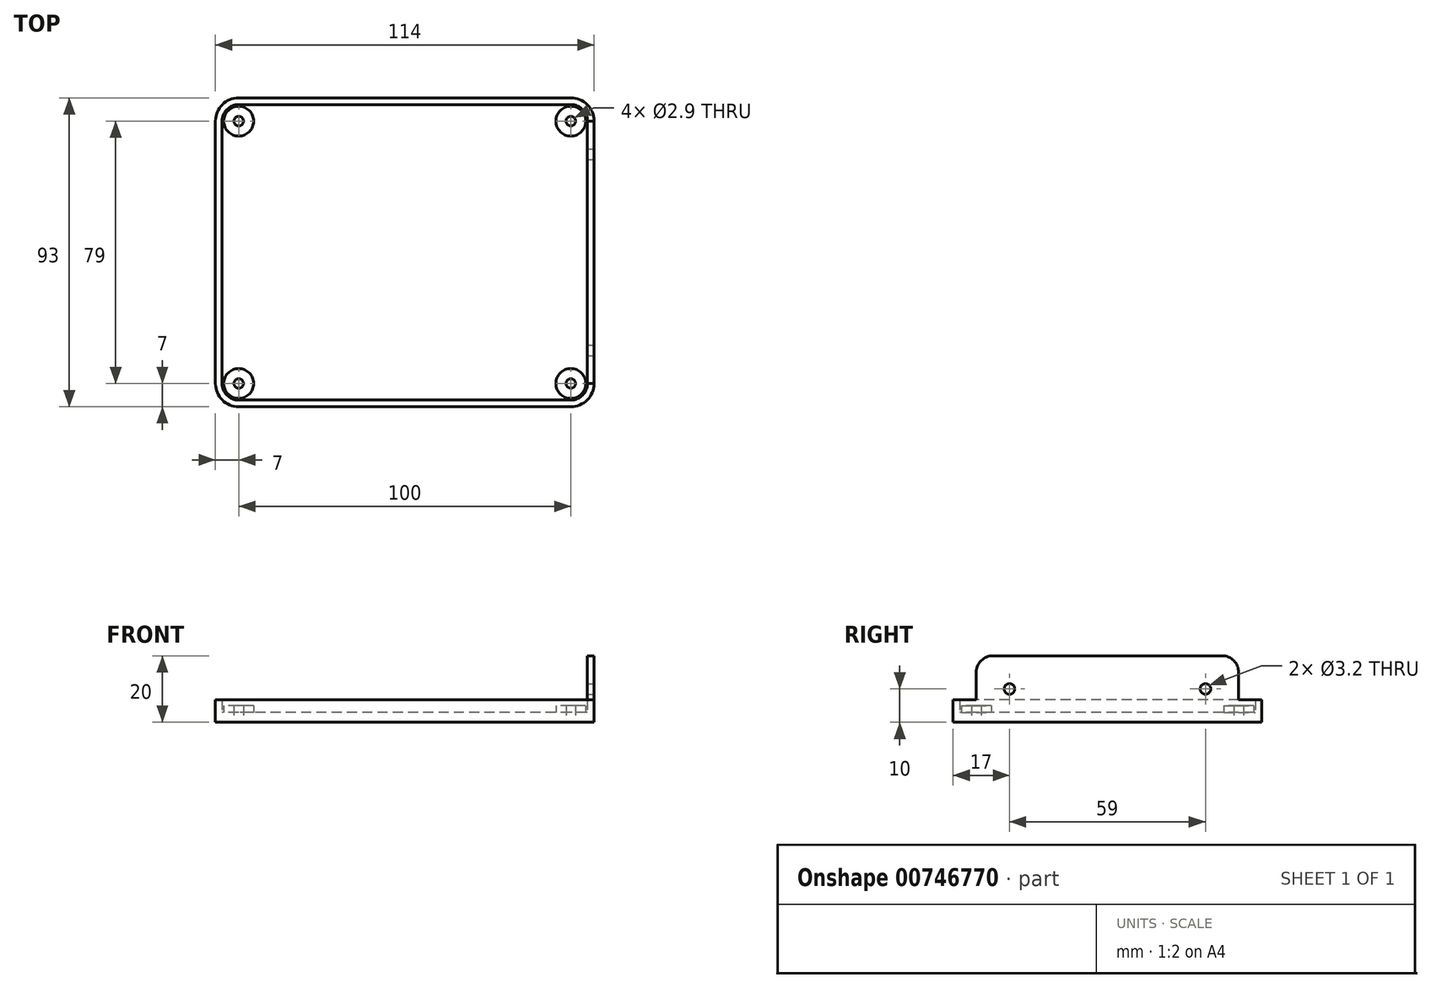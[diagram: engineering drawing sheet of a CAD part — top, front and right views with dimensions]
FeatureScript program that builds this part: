
annotation { "Feature Type Name" : "Feature", "Feature Type Description" : "" }
export const myFeature = defineFeature(function(context is Context, id is Id, definition is map)
    precondition{}
    {
        {
            var Q0;
            Q0=qCreatedBy(makeId("Top.planeOp"),FACE);
            var sketch = newSketch(context, id + "F0", { "sketchPlane" : qUnion([Q0])});
            skLineSegment(sketch, "E0.bottom", {"start": v(50, 44.5) * mm, "end": v(-50, 44.5) * mm});
            skLineSegment(sketch, "E0.top", {"start": v(50, -44.5) * mm, "end": v(-50, -44.5) * mm});
            skLineSegment(sketch, "E0.left", {"start": v(55, 39.5) * mm, "end": v(55, -39.5) * mm});
            skLineSegment(sketch, "E0.right", {"start": v(-55, 39.5) * mm, "end": v(-55, -39.5) * mm});
            skPoint(sketch, "E0.middle", {"position": v(0, 0) * mm});
            skCircle(sketch, "E1", {"center": v(-50, 39.5) * mm, "radius": 1.45 * mm});
            skCircle(sketch, "E2", {"center": v(-50, 39.5) * mm, "radius": 4.5 * mm});
            skCircle(sketch, "E3.0.1.0", {"center": v(-50, -39.5) * mm, "radius": 1.45 * mm});
            skCircle(sketch, "E3.0.1.1", {"center": v(-50, -39.5) * mm, "radius": 4.5 * mm});
            skCircle(sketch, "E3.1.0.0", {"center": v(50, 39.5) * mm, "radius": 1.45 * mm});
            skCircle(sketch, "E3.1.0.1", {"center": v(50, 39.5) * mm, "radius": 4.5 * mm});
            skCircle(sketch, "E3.1.1.0", {"center": v(50, -39.5) * mm, "radius": 1.45 * mm});
            skCircle(sketch, "E3.1.1.1", {"center": v(50, -39.5) * mm, "radius": 4.5 * mm});
            skLineSegment(sketch, "E3.direction1", {"start": v(-50, 39.5) * mm, "end": v(50, 39.5) * mm, "construction": true});
            skLineSegment(sketch, "E3.direction2", {"start": v(-50, 39.5) * mm, "end": v(-50, -39.5) * mm, "construction": true});
            skPoint(sketch, "E4.visualSharp", {"position": v(-55, 44.5) * mm});
            skArc(sketch, "E4.filletArc", {"start": v(-50, 44.5) * mm, "mid": v(-53.54, 43.04) * mm, "end": v(-55, 39.5) * mm});
            skPoint(sketch, "E5.visualSharp", {"position": v(55, 44.5) * mm});
            skArc(sketch, "E5.filletArc", {"start": v(55, 39.5) * mm, "mid": v(53.54, 43.04) * mm, "end": v(50, 44.5) * mm});
            skPoint(sketch, "E6.visualSharp", {"position": v(55, -44.5) * mm});
            skArc(sketch, "E6.filletArc", {"start": v(50, -44.5) * mm, "mid": v(53.54, -43.04) * mm, "end": v(55, -39.5) * mm});
            skPoint(sketch, "E7.visualSharp", {"position": v(-55, -44.5) * mm});
            skArc(sketch, "E7.filletArc", {"start": v(-55, -39.5) * mm, "mid": v(-53.54, -43.04) * mm, "end": v(-50, -44.5) * mm});
            skArc(sketch, "E8.0", {"start": v(57, 39.5) * mm, "mid": v(54.95, 44.45) * mm, "end": v(50, 46.5) * mm});
            skLineSegment(sketch, "E8.1", {"start": v(57, 39.5) * mm, "end": v(57, -39.5) * mm});
            skLineSegment(sketch, "E8.2", {"start": v(50, 46.5) * mm, "end": v(-50, 46.5) * mm});
            skArc(sketch, "E8.3", {"start": v(50, -46.5) * mm, "mid": v(54.95, -44.45) * mm, "end": v(57, -39.5) * mm});
            skArc(sketch, "E8.4", {"start": v(-50, 46.5) * mm, "mid": v(-54.95, 44.45) * mm, "end": v(-57, 39.5) * mm});
            skLineSegment(sketch, "E8.5", {"start": v(-57, 39.5) * mm, "end": v(-57, -39.5) * mm});
            skArc(sketch, "E8.6", {"start": v(-57, -39.5) * mm, "mid": v(-54.95, -44.45) * mm, "end": v(-50, -46.5) * mm});
            skLineSegment(sketch, "E8.7", {"start": v(50, -46.5) * mm, "end": v(-50, -46.5) * mm});
            skSolve(sketch);
        }
        {
            var Q0;
            Q0=makeQuery(id+"F0.imprint","IMPRINT",FACE,{"disambiguationData":[TD([[makeQuery(id+"F0.imprint","IMPRINT",EDGE,{"derivedFrom":sQuery(id+"F0.wireOp",EDGE,"E0.bottom")}),1.0]])]});
            var Q1;
            Q1=makeQuery(id+"F0.imprint","IMPRINT",FACE,{"disambiguationData":[TD([[makeQuery(id+"F0.imprint","IMPRINT",EDGE,{"derivedFrom":sQuery(id+"F0.wireOp",EDGE,"E3.1.1.0")}),-1.0]])]});
            var Q2;
            Q2=makeQuery(id+"F0.imprint","IMPRINT",FACE,{"disambiguationData":[TD([[makeQuery(id+"F0.imprint","IMPRINT",EDGE,{"derivedFrom":sQuery(id+"F0.wireOp",EDGE,"E3.1.0.0")}),-1.0]])]});
            var Q3;
            Q3=makeQuery(id+"F0.imprint","IMPRINT",FACE,{"disambiguationData":[TD([[makeQuery(id+"F0.imprint","IMPRINT",EDGE,{"derivedFrom":sQuery(id+"F0.wireOp",EDGE,"E3.0.1.0")}),-1.0]])]});
            var Q4;
            Q4=makeQuery(id+"F0.imprint","IMPRINT",FACE,{"disambiguationData":[TD([[makeQuery(id+"F0.imprint","IMPRINT",EDGE,{"derivedFrom":sQuery(id+"F0.wireOp",EDGE,"E1")}),-1.0]])]});
            extrude(context, id + "F1", {"entities" : qUnion([Q0, Q1, Q2, Q3, Q4]), "depth" : 3 * mm, "offsetDistance" : 25 * mm});
        }
        {
            var Q0;
            Q0=makeQuery(id+"F0.imprint","IMPRINT",FACE,{"disambiguationData":[TD([[makeQuery(id+"F0.imprint","IMPRINT",EDGE,{"derivedFrom":sQuery(id+"F0.wireOp",EDGE,"E1")}),-1.0]])]});
            var Q1;
            Q1=makeQuery(id+"F0.imprint","IMPRINT",FACE,{"disambiguationData":[TD([[makeQuery(id+"F0.imprint","IMPRINT",EDGE,{"derivedFrom":sQuery(id+"F0.wireOp",EDGE,"E3.0.1.0")}),-1.0]])]});
            var Q2;
            Q2=makeQuery(id+"F0.imprint","IMPRINT",FACE,{"disambiguationData":[TD([[makeQuery(id+"F0.imprint","IMPRINT",EDGE,{"derivedFrom":sQuery(id+"F0.wireOp",EDGE,"E3.1.1.0")}),-1.0]])]});
            var Q3;
            Q3=makeQuery(id+"F0.imprint","IMPRINT",FACE,{"disambiguationData":[TD([[makeQuery(id+"F0.imprint","IMPRINT",EDGE,{"derivedFrom":sQuery(id+"F0.wireOp",EDGE,"E3.1.0.0")}),-1.0]])]});
            extrude(context, id + "F2", {"entities" : qUnion([Q0, Q1, Q2, Q3]), "operationType" : NewBodyOperationType.ADD, "depth" : 5 * mm, "offsetDistance" : 25 * mm});
        }
        {
            var Q0;
            Q0=makeQuery(id+"F0.imprint","IMPRINT",FACE,{"disambiguationData":[TD([[makeQuery(id+"F0.imprint","IMPRINT",EDGE,{"derivedFrom":sQuery(id+"F0.wireOp",EDGE,"E0.bottom")}),-1.0]])]});
            extrude(context, id + "F3", {"entities" : qUnion([Q0]), "operationType" : NewBodyOperationType.ADD, "depth" : 6.7 * mm, "offsetDistance" : 25 * mm});
        }
        {
            var Q0;
            Q0=makeQuery(id+"F3.opExtrude","SWEPT_FACE",FACE,{"disambiguationData":[OSD([sQuery(id+"F0.wireOp",EDGE,"E8.1")])]});
            var sketch = newSketch(context, id + "F4", { "sketchPlane" : qUnion([Q0])});
            skLineSegment(sketch, "E9.bottom", {"start": v(-39.5, 0) * mm, "end": v(39.5, 0) * mm});
            skLineSegment(sketch, "E9.top", {"start": v(-39.5, 20) * mm, "end": v(39.5, 20) * mm});
            skLineSegment(sketch, "E9.left", {"start": v(-39.5, 0) * mm, "end": v(-39.5, 20) * mm});
            skLineSegment(sketch, "E9.right", {"start": v(39.5, 0) * mm, "end": v(39.5, 20) * mm});
            skLineSegment(sketch, "E10", {"start": v(0, 0) * mm, "end": v(0, 20) * mm, "construction": true});
            skCircle(sketch, "E11", {"center": v(-29.5, 10) * mm, "radius": 1.6 * mm});
            skCircle(sketch, "E12.MirrorC", {"center": v(29.5, 10) * mm, "radius": 1.6 * mm});
            skSolve(sketch);
        }
        {
            var Q0;
            {var subQ0=sQuery(id+"F4.wireOp",EDGE,"E9.top");Q0=makeQuery(id+"F4.imprint","IMPRINT",FACE,{"disambiguationData":[TD([[makeQuery(id+"F4.imprint","IMPRINT",EDGE,{"derivedFrom":subQ0}),-1.0]])]});}
            extrude(context, id + "F5", {"entities" : qUnion([Q0]), "operationType" : NewBodyOperationType.ADD, "oppositeDirection" : true, "depth" : 2 * mm, "offsetDistance" : 25 * mm});
        }
        {
            var Q0;
            Q0=makeQuery(id+"F5.opExtrude","SWEPT_EDGE",EDGE,{"disambiguationData":[OSD([sQuery(id+"F0.wireOp",EDGE,"E8.1"),sQuery(id+"F4.wireOp",EDGE,"E9.left")])]});
            var Q1;
            Q1=makeQuery(id+"F5.opExtrude","SWEPT_EDGE",EDGE,{"disambiguationData":[OSD([sQuery(id+"F4.wireOp",EDGE,"E9.top"),sQuery(id+"F4.wireOp",EDGE,"E9.left")])]});
            var Q2;
            Q2=makeQuery(id+"F5.opExtrude","SWEPT_EDGE",EDGE,{"disambiguationData":[OSD([sQuery(id+"F0.wireOp",EDGE,"E8.1"),sQuery(id+"F4.wireOp",EDGE,"E9.right")])]});
            var Q3;
            Q3=makeQuery(id+"F5.opExtrude","SWEPT_EDGE",EDGE,{"disambiguationData":[OSD([sQuery(id+"F4.wireOp",EDGE,"E9.top"),sQuery(id+"F4.wireOp",EDGE,"E9.right")])]});
            fillet(context, id + "F6", {"entities" : qUnion([Q0, Q1, Q2, Q3]), "radius" : 5 * mm, "tangentPropagation" : true, "allowEdgeOverflow" : false});
        }
    });
